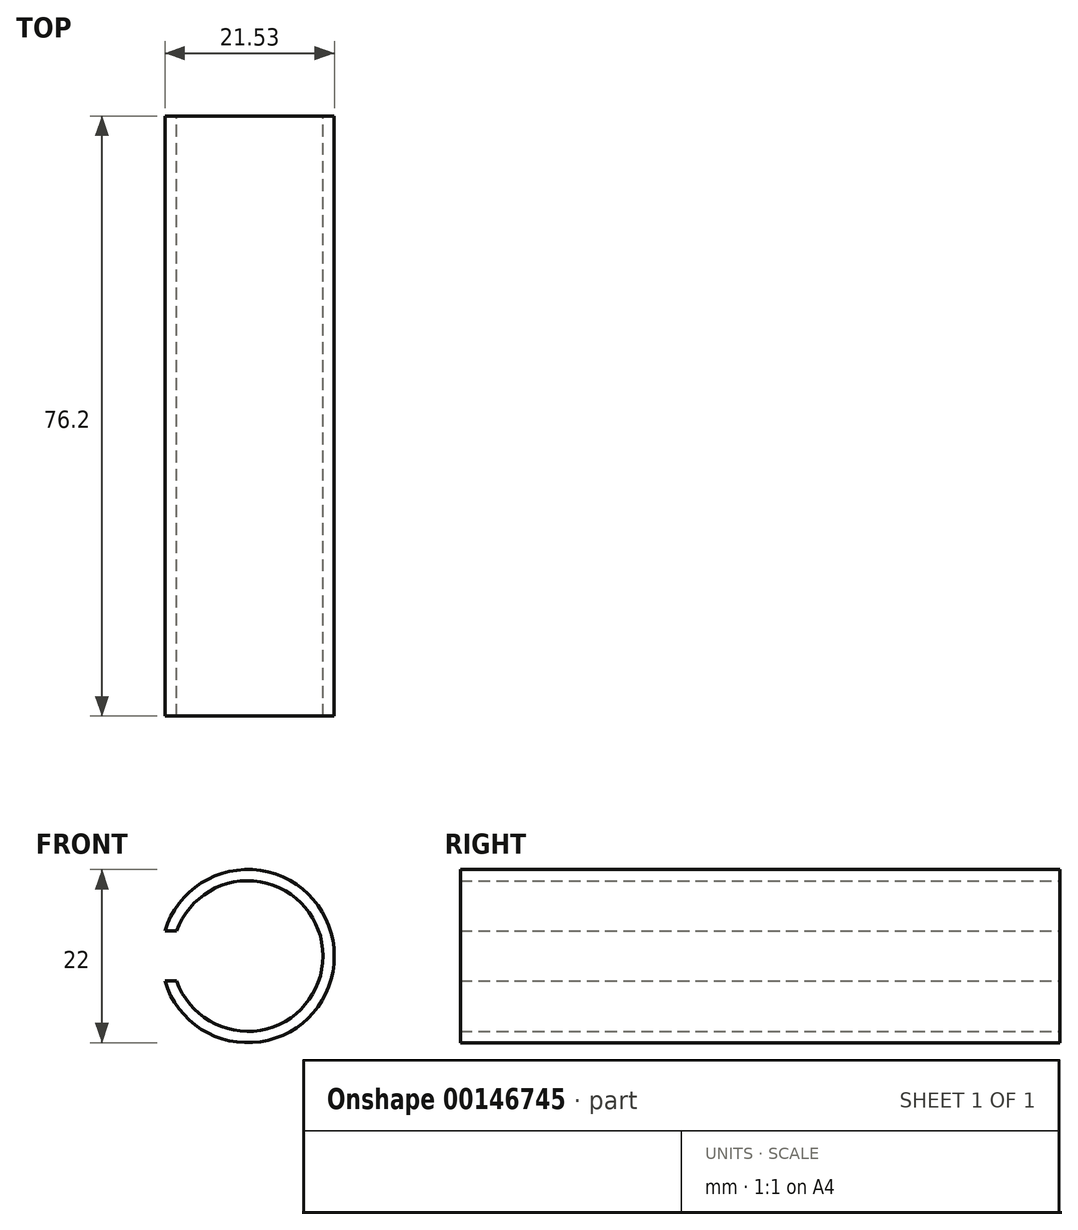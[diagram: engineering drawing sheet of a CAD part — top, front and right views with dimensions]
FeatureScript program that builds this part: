
annotation { "Feature Type Name" : "Feature", "Feature Type Description" : "" }
export const myFeature = defineFeature(function(context is Context, id is Id, definition is map)
    precondition{}
    {
        {
            var Q0;
            Q0=qCreatedBy(makeId("Front.planeOp"),FACE);
            var sketch = newSketch(context, id + "F0", { "sketchPlane" : qUnion([Q0])});
            skArc(sketch, "E0", {"start": v(-10.53, -3.17) * mm, "mid": v(11, 0) * mm, "end": v(-10.53, 3.18) * mm});
            skArc(sketch, "E1", {"start": v(-9.02, -3.17) * mm, "mid": v(9.56, 0) * mm, "end": v(-9.02, 3.18) * mm});
            skLineSegment(sketch, "E2.bottom", {"start": v(-13.92, 3.18) * mm, "end": v(-7.57, 3.18) * mm});
            skLineSegment(sketch, "E2.top", {"start": v(-13.92, -3.18) * mm, "end": v(-7.57, -3.18) * mm});
            skLineSegment(sketch, "E2.left", {"start": v(-13.92, 3.18) * mm, "end": v(-13.92, -3.18) * mm});
            skLineSegment(sketch, "E2.right", {"start": v(-7.57, 3.18) * mm, "end": v(-7.57, -3.18) * mm});
            skSolve(sketch);
        }
        {
            var Q0;
            Q0=makeQuery(id+"F0.imprint","IMPRINT",FACE,{"disambiguationData":[TD([[makeQuery(id+"F0.imprint","IMPRINT",EDGE,{"derivedFrom":sQuery(id+"F0.wireOp",EDGE,"E1")}),-1.0]])]});
            extrude(context, id + "F1", {"entities" : qUnion([Q0]), "endBound" : BoundingType.SYMMETRIC, "depth" : 76.2 * mm});
        }
    });
